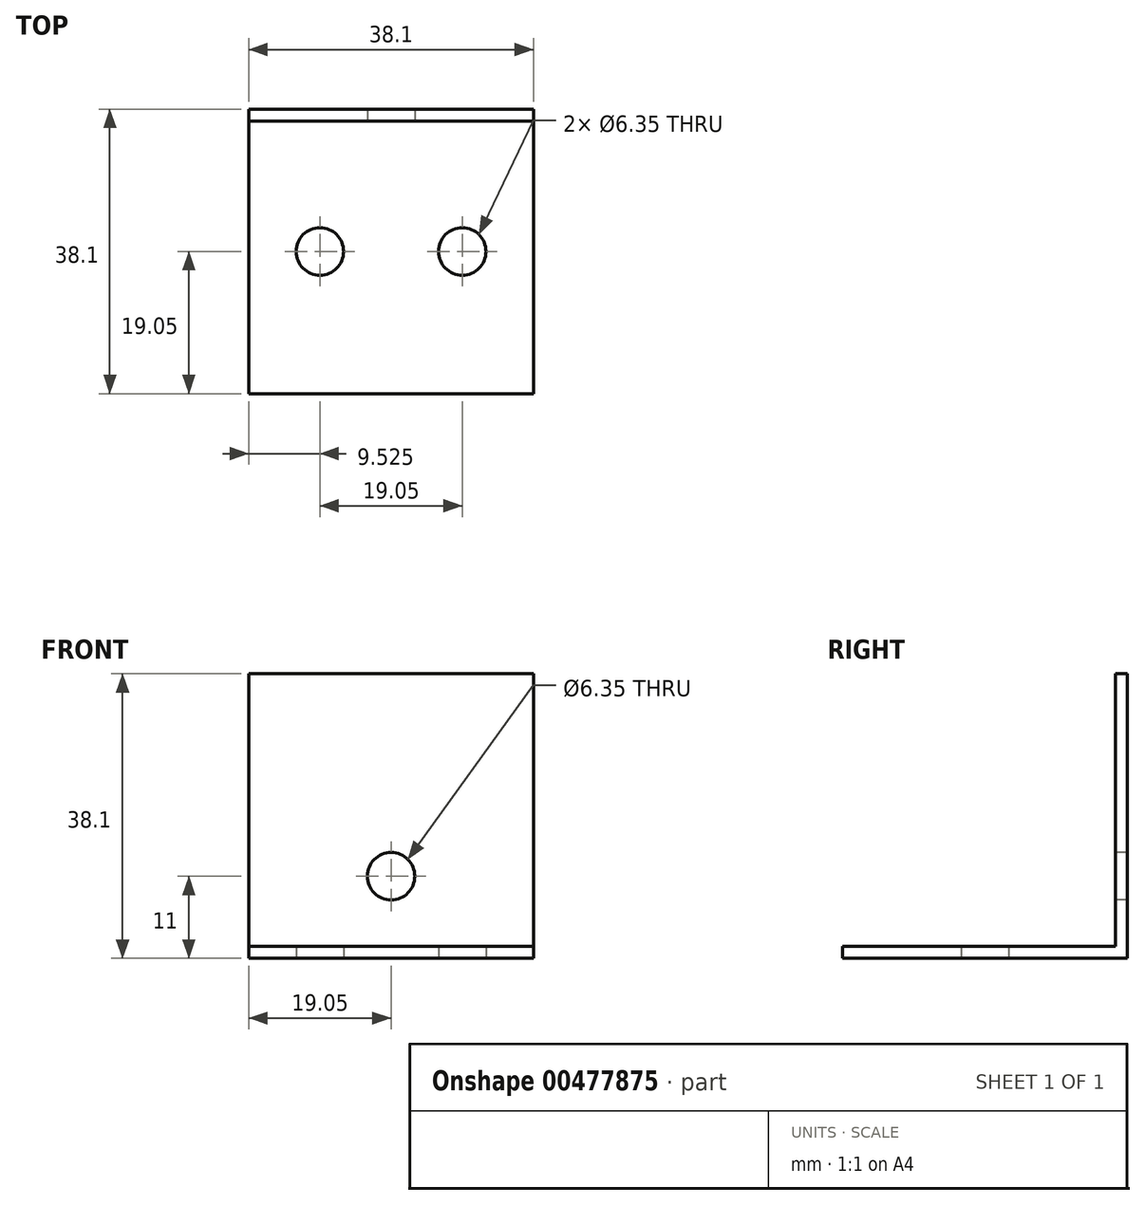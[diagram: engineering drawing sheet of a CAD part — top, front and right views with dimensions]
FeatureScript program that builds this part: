
annotation { "Feature Type Name" : "Feature", "Feature Type Description" : "" }
export const myFeature = defineFeature(function(context is Context, id is Id, definition is map)
    precondition{}
    {
        {
            var Q0;
            Q0=qCreatedBy(makeId("Right.planeOp"),FACE);
            var sketch = newSketch(context, id + "F0", { "sketchPlane" : qUnion([Q0])});
            skLineSegment(sketch, "E0.bottom", {"start": v(0, 0) * mm, "end": v(38.1, 0) * mm});
            skLineSegment(sketch, "E0.top", {"start": v(0, 1.59) * mm, "end": v(36.51, 1.59) * mm});
            skLineSegment(sketch, "E0.left", {"start": v(0, 0) * mm, "end": v(0, 1.59) * mm});
            skLineSegment(sketch, "E0.right", {"start": v(38.1, 0) * mm, "end": v(38.1, 1.59) * mm});
            skLineSegment(sketch, "E1", {"start": v(38.1, 1.59) * mm, "end": v(38.1, 38.1) * mm});
            skLineSegment(sketch, "E2", {"start": v(38.1, 38.1) * mm, "end": v(36.51, 38.1) * mm});
            skLineSegment(sketch, "E3", {"start": v(36.51, 38.1) * mm, "end": v(36.51, 1.59) * mm});
            skSolve(sketch);
        }
        {
            var Q0;
            Q0=makeQuery(id+"F0.imprint","IMPRINT",FACE,{"disambiguationData":[TD([[makeQuery(id+"F0.imprint","IMPRINT",EDGE,{"derivedFrom":sQuery(id+"F0.wireOp",EDGE,"E0.bottom")}),1.0]])]});
            extrude(context, id + "F1", {"entities" : qUnion([Q0]), "depth" : 38.1 * mm, "offsetDistance" : 25.4 * mm});
        }
        {
            var Q0;
            Q0=makeQuery(id+"F1.opExtrude","SWEPT_FACE",FACE,{"disambiguationData":[OSD([sQuery(id+"F0.wireOp",EDGE,"E3")])]});
            var sketch = newSketch(context, id + "F2", { "sketchPlane" : qUnion([Q0])});
            skLineSegment(sketch, "E4", {"start": v(19.05, 38.1) * mm, "end": v(19.05, 1.59) * mm, "construction": true});
            skLineSegment(sketch, "E5", {"start": v(0, 1.59) * mm, "end": v(0, 0) * mm});
            skLineSegment(sketch, "E6", {"start": v(0, 11) * mm, "end": v(38.1, 11) * mm, "construction": true});
            skPoint(sketch, "E7", {"position": v(19.05, 11) * mm});
            skSolve(sketch);
        }
        {
            var Q0;
            Q0=sQuery(id+"F2.wireOp",VERTEX,"E7");
            var Q1;
            Q1=makeQuery(id+"F1.opExtrude","SWEPT_BODY",BODY,{"disambiguationData":[OSD([sQuery(id+"F0.wireOp",EDGE,"E0.bottom"),sQuery(id+"F0.wireOp",EDGE,"E0.top"),sQuery(id+"F0.wireOp",EDGE,"E0.left"),sQuery(id+"F0.wireOp",EDGE,"E0.right"),sQuery(id+"F0.wireOp",EDGE,"E1"),sQuery(id+"F0.wireOp",EDGE,"E2"),sQuery(id+"F0.wireOp",EDGE,"E3")])]});
            hole(context, id + "F3", {"style" : HoleStyle.SIMPLE, "endStyle" : HoleEndStyle.THROUGH, "holeDiameter" : 6.35 * mm, "isTappedThrough" : true, "tappedDepth" : 12.7 * mm, "tapClearance" : 3, "locations" : qUnion([Q0]), "scope" : qUnion([Q1])});
        }
        {
            var Q0;
            Q0=makeQuery(id+"F1.opExtrude","SWEPT_FACE",FACE,{"disambiguationData":[OSD([sQuery(id+"F0.wireOp",EDGE,"E0.bottom")])]});
            var sketch = newSketch(context, id + "F4", { "sketchPlane" : qUnion([Q0])});
            skLineSegment(sketch, "E8", {"start": v(0, -19.05) * mm, "end": v(9.53, -19.05) * mm, "construction": true});
            skLineSegment(sketch, "E9", {"start": v(9.53, 0) * mm, "end": v(9.53, -38.1) * mm, "construction": true});
            skLineSegment(sketch, "E10", {"start": v(28.58, 0) * mm, "end": v(28.58, -38.1) * mm, "construction": true});
            skLineSegment(sketch, "E11.trimOffspring", {"start": v(28.58, -19.05) * mm, "end": v(38.1, -19.05) * mm, "construction": true});
            skLineSegment(sketch, "E12", {"start": v(9.53, -19.05) * mm, "end": v(28.58, -19.05) * mm, "construction": true});
            skSolve(sketch);
        }
        {
            var Q0;
            Q0=sQuery(id+"F4.wireOp",VERTEX,"E8.end");
            var Q1;
            Q1=sQuery(id+"F4.wireOp",VERTEX,"E12.end");
            var Q2;
            Q2=makeQuery(id+"F1.opExtrude","SWEPT_BODY",BODY,{"disambiguationData":[OSD([sQuery(id+"F0.wireOp",EDGE,"E0.bottom"),sQuery(id+"F0.wireOp",EDGE,"E0.top"),sQuery(id+"F0.wireOp",EDGE,"E0.left"),sQuery(id+"F0.wireOp",EDGE,"E0.right"),sQuery(id+"F0.wireOp",EDGE,"E1"),sQuery(id+"F0.wireOp",EDGE,"E2"),sQuery(id+"F0.wireOp",EDGE,"E3")])]});
            hole(context, id + "F5", {"style" : HoleStyle.SIMPLE, "endStyle" : HoleEndStyle.THROUGH, "holeDiameter" : 6.35 * mm, "isTappedThrough" : true, "tappedDepth" : 12.7 * mm, "tapClearance" : 3, "locations" : qUnion([Q0, Q1]), "scope" : qUnion([Q2])});
        }
    });
